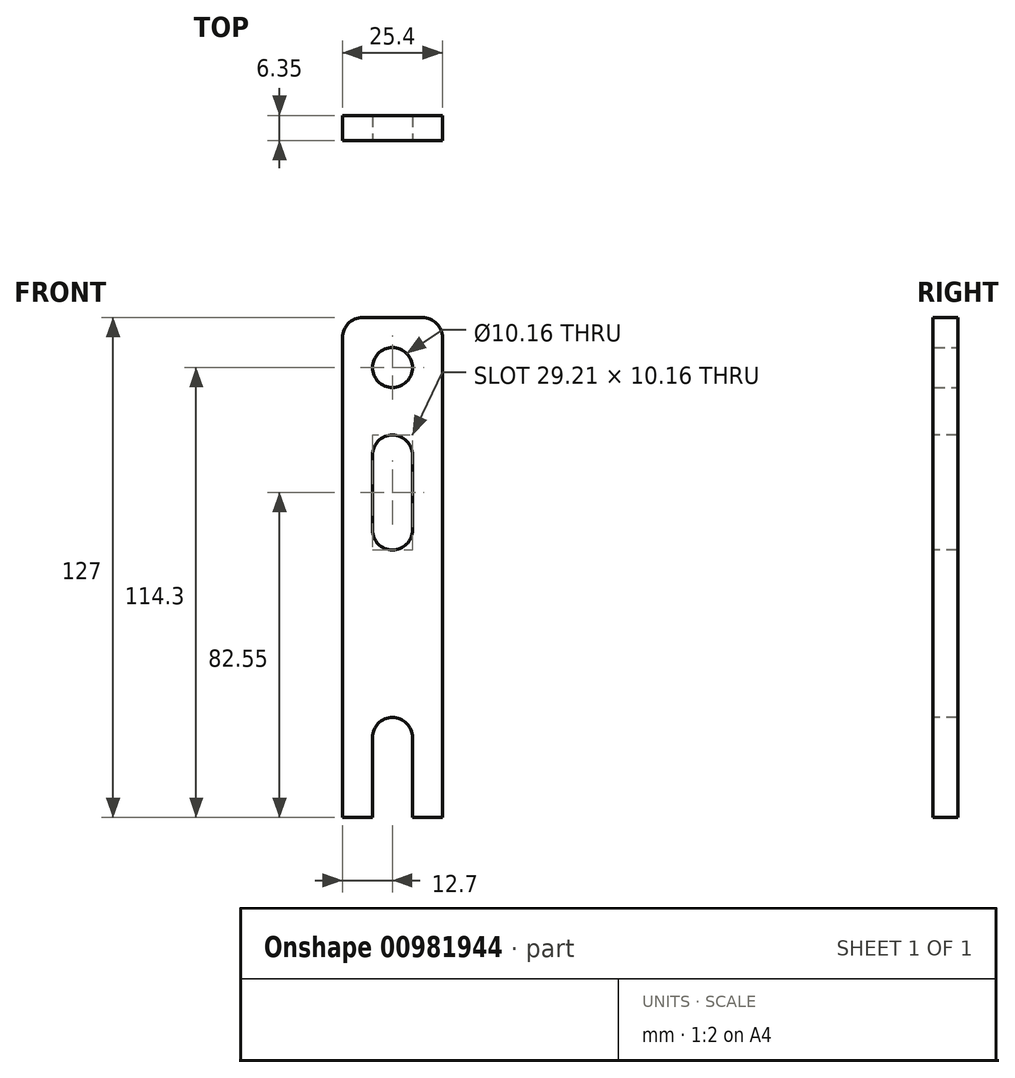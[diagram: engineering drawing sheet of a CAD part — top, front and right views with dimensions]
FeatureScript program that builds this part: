
annotation { "Feature Type Name" : "Feature", "Feature Type Description" : "" }
export const myFeature = defineFeature(function(context is Context, id is Id, definition is map)
    precondition{}
    {
        {
            var Q0;
            Q0=qCreatedBy(makeId("Front.planeOp"),FACE);
            var sketch = newSketch(context, id + "F0", { "sketchPlane" : qUnion([Q0])});
            skLineSegment(sketch, "E0.bottom", {"start": v(-12.7, 12.7) * mm, "end": v(12.7, 12.7) * mm});
            skLineSegment(sketch, "E0.top", {"start": v(-12.7, -114.3) * mm, "end": v(12.7, -114.3) * mm});
            skLineSegment(sketch, "E0.left", {"start": v(-12.7, 12.7) * mm, "end": v(-12.7, -114.3) * mm});
            skLineSegment(sketch, "E0.right", {"start": v(12.7, 12.7) * mm, "end": v(12.7, -114.3) * mm});
            skLineSegment(sketch, "E1", {"start": v(12.7, 12.7) * mm, "end": v(0, 0) * mm, "construction": true});
            skLineSegment(sketch, "E2", {"start": v(0, 0) * mm, "end": v(-12.7, 12.7) * mm, "construction": true});
            skCircle(sketch, "E3", {"center": v(0, 0) * mm, "radius": 5.08 * mm});
            skSolve(sketch);
        }
        {
            var Q0;
            Q0 = qSketchRegion(id + "F0", true);
            extrude(context, id + "F1", {"entities" : qUnion([Q0]), "depth" : 6.35 * mm, "offsetDistance" : 25.4 * mm});
        }
        {
            var Q0;
            Q0=makeQuery(id+"F1.opExtrude","SWEPT_EDGE",EDGE,{"disambiguationData":[OSD([sQuery(id+"F0.wireOp",EDGE,"E0.bottom"),sQuery(id+"F0.wireOp",EDGE,"E0.right")])]});
            var Q1;
            Q1=makeQuery(id+"F1.opExtrude","SWEPT_EDGE",EDGE,{"disambiguationData":[OSD([sQuery(id+"F0.wireOp",EDGE,"E0.bottom"),sQuery(id+"F0.wireOp",EDGE,"E0.left")])]});
            fillet(context, id + "F2", {"entities" : qUnion([Q0, Q1]), "radius" : 5.08 * mm, "tangentPropagation" : true, "allowEdgeOverflow" : false});
        }
        {
            var Q0;
            Q0=makeQuery(id+"F1.opExtrude","CAP_FACE",FACE,{"disambiguationData":[OSD([sQuery(id+"F0.wireOp",EDGE,"E0.bottom"),sQuery(id+"F0.wireOp",EDGE,"E0.top"),sQuery(id+"F0.wireOp",EDGE,"E0.left"),sQuery(id+"F0.wireOp",EDGE,"E0.right"),sQuery(id+"F0.wireOp",EDGE,"E3")])],"isStart":false});
            var sketch = newSketch(context, id + "F3", { "sketchPlane" : qUnion([Q0])});
            skLineSegment(sketch, "E4.bottom", {"start": v(5.08, -41.27) * mm, "end": v(-5.08, -41.27) * mm, "construction": true});
            skLineSegment(sketch, "E4.top", {"start": v(5.08, -22.22) * mm, "end": v(-5.08, -22.22) * mm, "construction": true});
            skLineSegment(sketch, "E4.left", {"start": v(5.08, -41.27) * mm, "end": v(5.08, -22.22) * mm});
            skLineSegment(sketch, "E4.right", {"start": v(-5.08, -41.27) * mm, "end": v(-5.08, -22.22) * mm});
            skPoint(sketch, "E4.middle", {"position": v(0, -31.75) * mm});
            skArc(sketch, "E5", {"start": v(5.08, -22.22) * mm, "mid": v(0, -17.14) * mm, "end": v(-5.08, -22.22) * mm});
            skArc(sketch, "E6", {"start": v(-5.08, -41.27) * mm, "mid": v(0, -46.35) * mm, "end": v(5.08, -41.27) * mm});
            skSolve(sketch);
        }
        {
            var Q0;
            Q0 = qSketchRegion(id + "F3", true);
            extrude(context, id + "F4", {"entities" : qUnion([Q0]), "operationType" : NewBodyOperationType.REMOVE, "oppositeDirection" : true, "depth" : 25.4 * mm, "offsetDistance" : 25.4 * mm});
        }
        {
            var Q0;
            Q0=makeQuery(id+"F1.opExtrude","CAP_FACE",FACE,{"disambiguationData":[OSD([sQuery(id+"F0.wireOp",EDGE,"E0.bottom"),sQuery(id+"F0.wireOp",EDGE,"E0.top"),sQuery(id+"F0.wireOp",EDGE,"E0.left"),sQuery(id+"F0.wireOp",EDGE,"E0.right"),sQuery(id+"F0.wireOp",EDGE,"E3")])],"isStart":false});
            var sketch = newSketch(context, id + "F5", { "sketchPlane" : qUnion([Q0])});
            skLineSegment(sketch, "E7.bottom", {"start": v(5.08, -114.3) * mm, "end": v(-5.08, -114.3) * mm});
            skLineSegment(sketch, "E7.top", {"start": v(5.08, -93.98) * mm, "end": v(-5.08, -93.98) * mm, "construction": true});
            skLineSegment(sketch, "E7.left", {"start": v(5.08, -114.3) * mm, "end": v(5.08, -93.98) * mm});
            skLineSegment(sketch, "E7.right", {"start": v(-5.08, -114.3) * mm, "end": v(-5.08, -93.98) * mm});
            skPoint(sketch, "E7.middle.positionSnap0", {"position": v(0, -46.35) * mm});
            skPoint(sketch, "E7.centerSnap0", {"position": v(0, -46.35) * mm});
            skLineSegment(sketch, "E8", {"start": v(0, -46.35) * mm, "end": v(0, -93.98) * mm, "construction": true});
            skArc(sketch, "E9", {"start": v(5.08, -93.98) * mm, "mid": v(0, -88.9) * mm, "end": v(-5.08, -93.98) * mm});
            skSolve(sketch);
        }
        {
            var Q0;
            Q0 = qSketchRegion(id + "F5", true);
            extrude(context, id + "F6", {"entities" : qUnion([Q0]), "operationType" : NewBodyOperationType.REMOVE, "endBound" : BoundingType.THROUGH_ALL, "oppositeDirection" : true, "depth" : 25.4 * mm, "offsetDistance" : 25.4 * mm});
        }
    });
